# Revit family: 1210_HRIS_nailfin_HP
name_source: partatom
category: Doors
revit_build: Autodesk Revit 2016 (Build: 20190507_1515(x64)
units: mm (PartAtom-declared; Revit-internal decimal feet)

## family parameters
Always vertical = Yes
Cut with Voids When Loaded = No
Host = Wall
OmniClass Number = 23.30.20.00
OmniClass Title = Windows
Room Calculation Point = No
Shared = No

## types (20) — shared parameters
Closed = No
Default Sill Height = 0"
Open = Yes
Setback = 1 1/8"
Wall Closure = By host

## per-type parameters (varying)
| type | Height | Sash Width | Width_x |
| 23X80Min | 80" | 20" | 23" |
| 23X86 | 86" | 20" | 23" |
| 23X92 | 92" | 20" | 23" |
| 23X96 | 96" | 20" | 23" |
| 30X80 | 80" | 27" | 30" |
| 30X86 | 86" | 27" | 30" |
| 30X92 | 92" | 27" | 30" |
| 30X96 | 96" | 27" | 30" |
| 36X80 | 80" | 33" | 36" |
| 36X86 | 86" | 33" | 36" |
| 36X92 | 92" | 33" | 36" |
| 36X96 | 96" | 33" | 36" |
| 41X80 | 80" | 38" | 41" |
| 41X86 | 86" | 38" | 41" |
| 41X92 | 92" | 38" | 41" |
| 41X96Max | 96" | 38" | 41" |
| 40X80 | 80" | 37" | 40" |
| 40X86 | 86" | 37" | 40" |
| 40X92 | 92" | 37" | 40" |
| 40X96 | 96" | 37" | 40" |

## geometry (parser evidence)
native form markers: Sweep x4
no freeform markers — native parametric forms only
